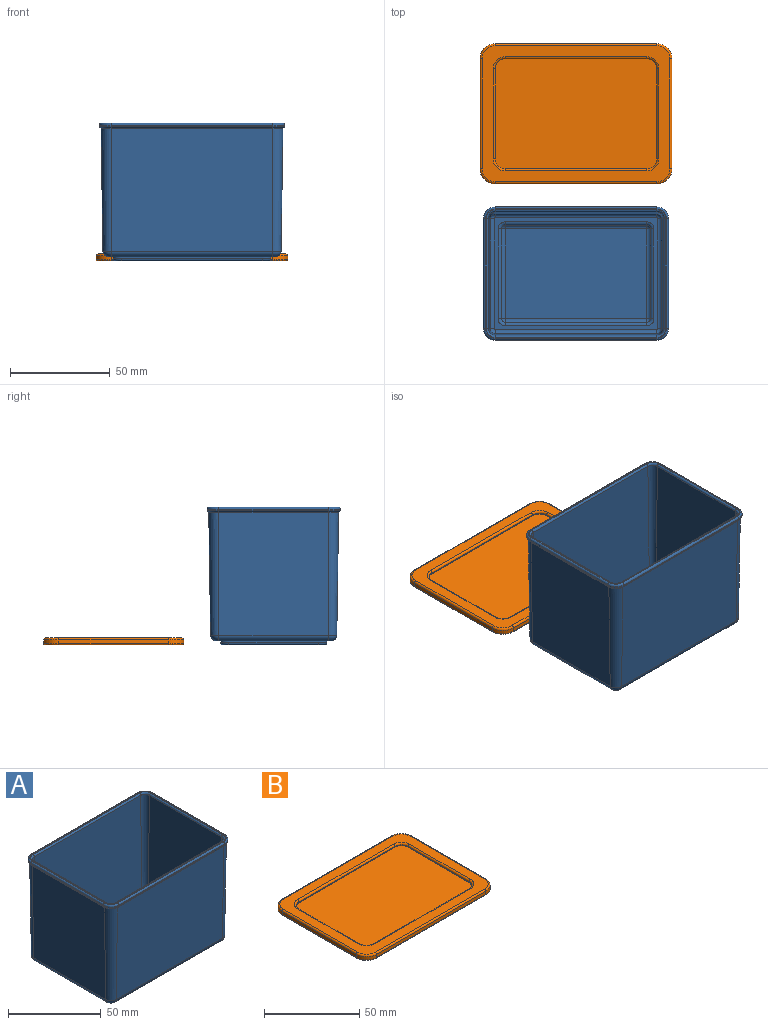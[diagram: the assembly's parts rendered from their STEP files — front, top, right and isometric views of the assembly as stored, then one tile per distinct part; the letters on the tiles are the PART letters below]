
ASSEMBLY  parts=2 mates=1
PART A: 101 faces, bbox 93.6x67.6x69 mm
  f0: plane 81.91x55.91mm, normal (0,0,1), area 542.6mm2, adj f37,f38,f39,f40,f41,f42,f43,f44
  f1: plane 83.09x57.09mm, normal (0,0,-1), area 569.2mm2, adj f12,f13,f14,f23,f24,f31,f32,f36
  f2: plane 90.6x64.6mm, normal (0,0,1), area 124.9mm2, adj f61,f62,f63,f64,f65,f66,f67,f68
  f3: plane 81x61.54mm, normal (0,1,-0.01), area 4985.7mm2, adj f4,f17,f45,f57
  f4: cone r=4mm half-angle=0.9deg, axis (0,0,1), area 435.4mm2, adj f3,f5,f47,f55
  f5: plane 61.54x55mm, normal (-1,0,-0.01), area 3385.3mm2, adj f4,f26,f49,f53
  f6: plane 81x62.44mm, normal (0,-1,0.01), area 5058.6mm2, adj f7,f19,f37,f69
  f7: cone r=2.4mm half-angle=0.9deg, axis (0,0,1), area 286.4mm2, adj f6,f8,f39,f71
  f8: plane 62.44x55mm, normal (1,0,0.01), area 3434.8mm2, adj f7,f28,f41,f73
  f9: plane 55x0.51mm, normal (-1,0,0), area 28.2mm2, adj f10,f29,f53,f61
  f10: cylinder r=5.8mm len=5.8mm, axis (0,0,-1), area 4.7mm2, adj f9,f11,f55,f63
  f11: plane 81x0.51mm, normal (0,1,0), area 41.6mm2, adj f10,f22,f57,f65
  f12: cylinder r=4mm len=4mm, axis (0,0,1), area 6.3mm2, adj f1,f13,f14,f79
  f13: plane 71x1mm, normal (0,1,0), area 71mm2, adj f1,f12,f23,f81
  f14: plane 45x1mm, normal (-1,0,0), area 45mm2, adj f1,f12,f31,f77
  f15: plane 77x51mm, normal (0,0,-1), area 3919.3mm2, adj f77,f78,f79,f80,f81,f82,f83,f84
  f16: plane 71x45mm, normal (0,0,1), area 3195mm2, adj f85,f88,f89,f92
  f17: cone r=4mm half-angle=0.9deg, axis (0,0,1), area 435.4mm2, adj f3,f18,f46,f59
  f18: plane 61.54x55mm, normal (1,0,-0.01), area 3385.3mm2, adj f17,f33,f48,f60
  f19: cone r=2.4mm half-angle=0.9deg, axis (0,0,1), area 286.4mm2, adj f6,f20,f38,f70
  f20: plane 62.44x55mm, normal (-1,0,0.01), area 3434.8mm2, adj f19,f34,f40,f72
  f21: plane 55x0.51mm, normal (1,0,0), area 28.2mm2, adj f22,f35,f60,f68
  f22: cylinder r=5.8mm len=5.8mm, axis (0,0,-1), area 4.7mm2, adj f11,f21,f59,f67
  f23: cylinder r=4mm len=4mm, axis (0,0,1), area 6.3mm2, adj f1,f13,f24,f83
  f24: plane 45x1mm, normal (1,0,0), area 45mm2, adj f1,f23,f36,f84
  f25: plane 81x61.54mm, normal (0,-1,-0.01), area 4985.7mm2, adj f26,f33,f52,f56
  f26: cone r=4mm half-angle=0.9deg, axis (0,0,1), area 435.4mm2, adj f5,f25,f51,f54
  f27: plane 81x62.44mm, normal (0,1,0.01), area 5058.6mm2, adj f28,f34,f44,f76
  f28: cone r=2.4mm half-angle=0.9deg, axis (0,0,1), area 286.4mm2, adj f8,f27,f43,f75
  f29: cylinder r=5.8mm len=5.8mm, axis (0,0,-1), area 4.7mm2, adj f9,f30,f54,f62
  f30: plane 81x0.51mm, normal (0,-1,0), area 41.6mm2, adj f29,f35,f56,f64
  f31: cylinder r=4mm len=4mm, axis (0,0,1), area 6.3mm2, adj f1,f14,f32,f78
  f32: plane 71x1mm, normal (0,-1,0), area 71mm2, adj f1,f31,f36,f80
  f33: cone r=4mm half-angle=0.9deg, axis (0,0,1), area 435.4mm2, adj f18,f25,f50,f58
  f34: cone r=2.4mm half-angle=0.9deg, axis (0,0,1), area 286.4mm2, adj f20,f27,f42,f74
  f35: cylinder r=5.8mm len=5.8mm, axis (0,0,-1), area 4.7mm2, adj f21,f30,f58,f66
  f36: cylinder r=4mm len=4mm, axis (0,0,1), area 6.3mm2, adj f1,f24,f32,f82
  f37: cylinder r=2mm len=81mm, axis (-1,0,0), area 252.1mm2, adj f0,f6,f38,f39
  f38: torus R=0.45mm, axis (0,0,1), area 8.4mm2, adj f0,f19,f37,f40
  f39: torus R=0.45mm, axis (0,0,1), area 8.4mm2, adj f0,f7,f37,f41
  f40: cylinder r=2mm len=55mm, axis (0,1,0), area 171.1mm2, adj f0,f20,f38,f42
  f41: cylinder r=2mm len=55mm, axis (0,1,0), area 171.1mm2, adj f0,f8,f39,f43
  f42: torus R=0.45mm, axis (0,0,1), area 8.4mm2, adj f0,f34,f40,f44
  f43: torus R=0.45mm, axis (0,0,1), area 8.4mm2, adj f0,f28,f41,f44
  f44: cylinder r=2mm len=81mm, axis (-1,0,0), area 252.1mm2, adj f0,f27,f42,f43
  f45: cylinder r=3mm len=81mm, axis (1,0,0), area 378.1mm2, adj f1,f3,f46,f47
  f46: torus R=1.04mm, axis (0,0,1), area 21.6mm2, adj f1,f17,f45,f48
  f47: torus R=1.04mm, axis (0,0,1), area 21.6mm2, adj f1,f4,f45,f49
  f48: cylinder r=3mm len=55mm, axis (0,-1,0), area 256.7mm2, adj f1,f18,f46,f50
  f49: cylinder r=3mm len=55mm, axis (0,-1,0), area 256.7mm2, adj f1,f5,f47,f51
  f50: torus R=1.04mm, axis (0,0,1), area 21.6mm2, adj f1,f33,f48,f52
  f51: torus R=1.04mm, axis (0,0,1), area 21.6mm2, adj f1,f26,f49,f52
  f52: cylinder r=3mm len=81mm, axis (1,0,0), area 378.1mm2, adj f1,f25,f50,f51
  f53: cylinder r=1mm len=55mm, axis (0,-1,0), area 77.4mm2, adj f5,f9,f54,f55
  f54: torus R=4.8mm, axis (0,0,-1), area 12.2mm2, adj f26,f29,f53,f56
  f55: torus R=4.8mm, axis (0,0,-1), area 12.2mm2, adj f4,f10,f53,f57
  f56: cylinder r=1mm len=81mm, axis (-1,0,0), area 114mm2, adj f25,f30,f54,f58
  f57: cylinder r=1mm len=81mm, axis (1,0,0), area 114mm2, adj f3,f11,f55,f59
  f58: torus R=4.8mm, axis (0,0,-1), area 12.2mm2, adj f33,f35,f56,f60
  f59: torus R=4.8mm, axis (0,0,-1), area 12.2mm2, adj f17,f22,f57,f60
  f60: cylinder r=1mm len=55mm, axis (0,1,0), area 77.4mm2, adj f18,f21,f58,f59
  f61: cylinder r=1mm len=55mm, axis (0,1,0), area 86.4mm2, adj f2,f9,f62,f63
  f62: torus R=4.8mm, axis (0,0,1), area 13.4mm2, adj f2,f29,f61,f64
  f63: torus R=4.8mm, axis (0,0,1), area 13.4mm2, adj f2,f10,f61,f65
  f64: cylinder r=1mm len=81mm, axis (1,0,0), area 127.2mm2, adj f2,f30,f62,f66
  f65: cylinder r=1mm len=81mm, axis (1,0,0), area 127.2mm2, adj f2,f11,f63,f67
  f66: torus R=4.8mm, axis (0,0,1), area 13.4mm2, adj f2,f35,f64,f68
  f67: torus R=4.8mm, axis (0,0,1), area 13.4mm2, adj f2,f22,f65,f68
  f68: cylinder r=1mm len=55mm, axis (0,1,0), area 86.4mm2, adj f2,f21,f66,f67
  f69: cylinder r=1mm len=81mm, axis (1,0,0), area 126mm2, adj f2,f6,f70,f71
  f70: torus R=4.39mm, axis (0,0,1), area 9.2mm2, adj f2,f19,f69,f72
  f71: torus R=4.39mm, axis (0,0,1), area 9.2mm2, adj f2,f7,f69,f73
  f72: cylinder r=1mm len=55mm, axis (0,-1,0), area 85.6mm2, adj f2,f20,f70,f74
  f73: cylinder r=1mm len=55mm, axis (0,-1,0), area 85.6mm2, adj f2,f8,f71,f75
  f74: torus R=4.39mm, axis (0,0,1), area 9.2mm2, adj f2,f34,f72,f76
  f75: torus R=4.39mm, axis (0,0,1), area 9.2mm2, adj f2,f28,f73,f76
  f76: cylinder r=1mm len=81mm, axis (1,0,0), area 126mm2, adj f2,f27,f74,f75
  f77: cylinder r=1mm len=45mm, axis (0,-1,0), area 70.7mm2, adj f14,f15,f78,f79
  f78: torus R=3mm, axis (0,0,-1), area 9mm2, adj f15,f31,f77,f80
  f79: torus R=3mm, axis (0,0,-1), area 9mm2, adj f12,f15,f77,f81
  f80: cylinder r=1mm len=71mm, axis (-1,0,0), area 111.5mm2, adj f15,f32,f78,f82
  f81: cylinder r=1mm len=71mm, axis (-1,0,0), area 111.5mm2, adj f13,f15,f79,f83
  f82: torus R=3mm, axis (0,0,-1), area 9mm2, adj f15,f36,f80,f84
  f83: torus R=3mm, axis (0,0,-1), area 9mm2, adj f15,f23,f81,f84
  f84: cylinder r=1mm len=45mm, axis (0,-1,0), area 70.7mm2, adj f15,f24,f82,f83
  f85: cylinder r=2mm len=71mm, axis (-1,0,0), area 148.7mm2, adj f16,f86,f87,f93
  f86: sphere r=2mm, area 3.1mm2, adj f85,f88,f94
  f87: sphere r=2mm, area 3.1mm2, adj f85,f89,f95
  f88: cylinder r=2mm len=45mm, axis (0,-1,0), area 94.2mm2, adj f16,f86,f90,f96
  f89: cylinder r=2mm len=45mm, axis (0,-1,0), area 94.2mm2, adj f16,f87,f91,f97
  f90: sphere r=2mm, area 3.1mm2, adj f88,f92,f98
  f91: sphere r=2mm, area 3.1mm2, adj f89,f92,f99
  f92: cylinder r=2mm len=71mm, axis (-1,0,0), area 148.7mm2, adj f16,f90,f91,f100
  f93: cylinder r=2mm len=71mm, axis (-1,0,0), area 148.7mm2, adj f0,f85,f94,f95
  f94: torus R=3.46mm, axis (0,0,1), area 8.3mm2, adj f0,f86,f93,f96
  f95: torus R=3.46mm, axis (0,0,1), area 8.3mm2, adj f0,f87,f93,f97
  f96: cylinder r=2mm len=45mm, axis (0,-1,0), area 94.2mm2, adj f0,f88,f94,f98
  f97: cylinder r=2mm len=45mm, axis (0,-1,0), area 94.2mm2, adj f0,f89,f95,f99
  f98: torus R=3.46mm, axis (0,0,1), area 8.3mm2, adj f0,f90,f96,f100
  f99: torus R=3.46mm, axis (0,0,1), area 8.3mm2, adj f0,f91,f97,f100
  f100: cylinder r=2mm len=71mm, axis (-1,0,0), area 148.7mm2, adj f0,f92,f98,f99
PART B: 61 faces, bbox 97.2x71.2x3.5 mm
  f0: plane 94x68mm, normal (0,0,-1), area 1382.8mm2, adj f5,f6,f7,f9,f10,f11,f19,f20
  f1: plane 81x2mm, normal (0,1,0), area 162mm2, adj f2,f17,f41,f49
  f2: cylinder r=7.5mm len=7.5mm, axis (0,0,-1), area 23.6mm2, adj f1,f3,f39,f47
  f3: plane 55x2mm, normal (-1,0,0), area 110mm2, adj f2,f26,f37,f45
  f4: plane 94x68mm, normal (0,0,1), area 1655.6mm2, adj f37,f38,f39,f40,f41,f42,f43,f44
  f5: plane 81x2.5mm, normal (0,-1,0), area 202.5mm2, adj f0,f6,f8,f19
  f6: cylinder r=6.5mm len=6.5mm, axis (0,0,1), area 25.5mm2, adj f0,f5,f7,f8
  f7: plane 55x2.5mm, normal (1,0,0), area 137.5mm2, adj f0,f6,f8,f28
  f8: plane 95x69mm, normal (0,0,-1), area 157.2mm2, adj f5,f6,f7,f19,f20,f27,f28,f34
  f9: plane 71x2.5mm, normal (0,1,0), area 177.5mm2, adj f0,f11,f12,f22
  f10: plane 45x2.5mm, normal (-1,0,0), area 112.5mm2, adj f0,f11,f12,f30
  f11: cylinder r=7mm len=7mm, axis (0,0,1), area 27.5mm2, adj f0,f9,f10,f12
  f12: plane 85x59mm, normal (0,0,-1), area 4972.9mm2, adj f9,f10,f11,f21,f22,f29,f30,f35
  f13: plane 71x0.5mm, normal (0,-1,0), area 35.5mm2, adj f14,f16,f23,f53
  f14: cylinder r=5mm len=5mm, axis (0,0,1), area 3.9mm2, adj f13,f15,f16,f54
  f15: plane 45x0.5mm, normal (1,0,0), area 22.5mm2, adj f14,f16,f32,f56
  f16: plane 81x55mm, normal (0,0,1), area 4433.5mm2, adj f13,f14,f15,f23,f24,f31,f32,f36
  f17: cylinder r=7.5mm len=7.5mm, axis (0,0,-1), area 23.6mm2, adj f1,f18,f43,f51
  f18: plane 55x2mm, normal (1,0,0), area 110mm2, adj f17,f33,f44,f52
  f19: cylinder r=6.5mm len=6.5mm, axis (0,0,1), area 25.5mm2, adj f0,f5,f8,f20
  f20: plane 55x2.5mm, normal (-1,0,0), area 137.5mm2, adj f0,f8,f19,f34
  f21: plane 45x2.5mm, normal (1,0,0), area 112.5mm2, adj f0,f12,f22,f35
  f22: cylinder r=7mm len=7mm, axis (0,0,1), area 27.5mm2, adj f0,f9,f12,f21
  f23: cylinder r=5mm len=5mm, axis (0,0,1), area 3.9mm2, adj f13,f16,f24,f55
  f24: plane 45x0.5mm, normal (-1,0,0), area 22.5mm2, adj f16,f23,f36,f57
  f25: plane 81x2mm, normal (0,-1,0), area 162mm2, adj f26,f33,f40,f48
  f26: cylinder r=7.5mm len=7.5mm, axis (0,0,-1), area 23.6mm2, adj f3,f25,f38,f46
  f27: plane 81x2.5mm, normal (0,1,0), area 202.5mm2, adj f0,f8,f28,f34
  f28: cylinder r=6.5mm len=6.5mm, axis (0,0,1), area 25.5mm2, adj f0,f7,f8,f27
  f29: plane 71x2.5mm, normal (0,-1,0), area 177.5mm2, adj f0,f12,f30,f35
  f30: cylinder r=7mm len=7mm, axis (0,0,1), area 27.5mm2, adj f0,f10,f12,f29
  f31: plane 71x0.5mm, normal (0,1,0), area 35.5mm2, adj f16,f32,f36,f60
  f32: cylinder r=5mm len=5mm, axis (0,0,1), area 3.9mm2, adj f15,f16,f31,f58
  f33: cylinder r=7.5mm len=7.5mm, axis (0,0,-1), area 23.6mm2, adj f18,f25,f42,f50
  f34: cylinder r=6.5mm len=6.5mm, axis (0,0,1), area 25.5mm2, adj f0,f8,f20,f27
  f35: cylinder r=7mm len=7mm, axis (0,0,1), area 27.5mm2, adj f0,f12,f21,f29
  f36: cylinder r=5mm len=5mm, axis (0,0,1), area 3.9mm2, adj f16,f24,f31,f59
  f37: cylinder r=1mm len=55mm, axis (0,1,0), area 86.4mm2, adj f3,f4,f38,f39
  f38: torus R=6.5mm, axis (0,0,1), area 17.6mm2, adj f4,f26,f37,f40
  f39: torus R=6.5mm, axis (0,0,1), area 17.6mm2, adj f2,f4,f37,f41
  f40: cylinder r=1mm len=81mm, axis (1,0,0), area 127.2mm2, adj f4,f25,f38,f42
  f41: cylinder r=1mm len=81mm, axis (1,0,0), area 127.2mm2, adj f1,f4,f39,f43
  f42: torus R=6.5mm, axis (0,0,1), area 17.6mm2, adj f4,f33,f40,f44
  f43: torus R=6.5mm, axis (0,0,1), area 17.6mm2, adj f4,f17,f41,f44
  f44: cylinder r=1mm len=55mm, axis (0,1,0), area 86.4mm2, adj f4,f18,f42,f43
  f45: cylinder r=0.5mm len=55mm, axis (0,1,0), area 43.2mm2, adj f3,f8,f46,f47
  f46: torus R=7mm, axis (0,0,-1), area 9mm2, adj f8,f26,f45,f48
  f47: torus R=7mm, axis (0,0,-1), area 9mm2, adj f2,f8,f45,f49
  f48: cylinder r=0.5mm len=81mm, axis (1,0,0), area 63.6mm2, adj f8,f25,f46,f50
  f49: cylinder r=0.5mm len=81mm, axis (1,0,0), area 63.6mm2, adj f1,f8,f47,f51
  f50: torus R=7mm, axis (0,0,-1), area 9mm2, adj f8,f33,f48,f52
  f51: torus R=7mm, axis (0,0,-1), area 9mm2, adj f8,f17,f49,f52
  f52: cylinder r=0.5mm len=55mm, axis (0,1,0), area 43.2mm2, adj f8,f18,f50,f51
  f53: cylinder r=1mm len=71mm, axis (1,0,0), area 111.5mm2, adj f4,f13,f54,f55
  f54: torus R=6mm, axis (0,0,1), area 13.2mm2, adj f4,f14,f53,f56
  f55: torus R=6mm, axis (0,0,1), area 13.2mm2, adj f4,f23,f53,f57
  f56: cylinder r=1mm len=45mm, axis (0,1,0), area 70.7mm2, adj f4,f15,f54,f58
  f57: cylinder r=1mm len=45mm, axis (0,1,0), area 70.7mm2, adj f4,f24,f55,f59
  f58: torus R=6mm, axis (0,0,1), area 13.2mm2, adj f4,f32,f56,f60
  f59: torus R=6mm, axis (0,0,1), area 13.2mm2, adj f4,f36,f57,f60
  f60: cylinder r=1mm len=71mm, axis (1,0,0), area 111.5mm2, adj f4,f31,f58,f59
PLACE A t=(-3.22,6.79,-20.03)mm fixed
PLACE B t=(-3.22,86.79,-86.53)mm
MATE planar A.f15 <-> B.f12  axis (0,0,-1) through (-3.22,6.79,-22.03)mm
